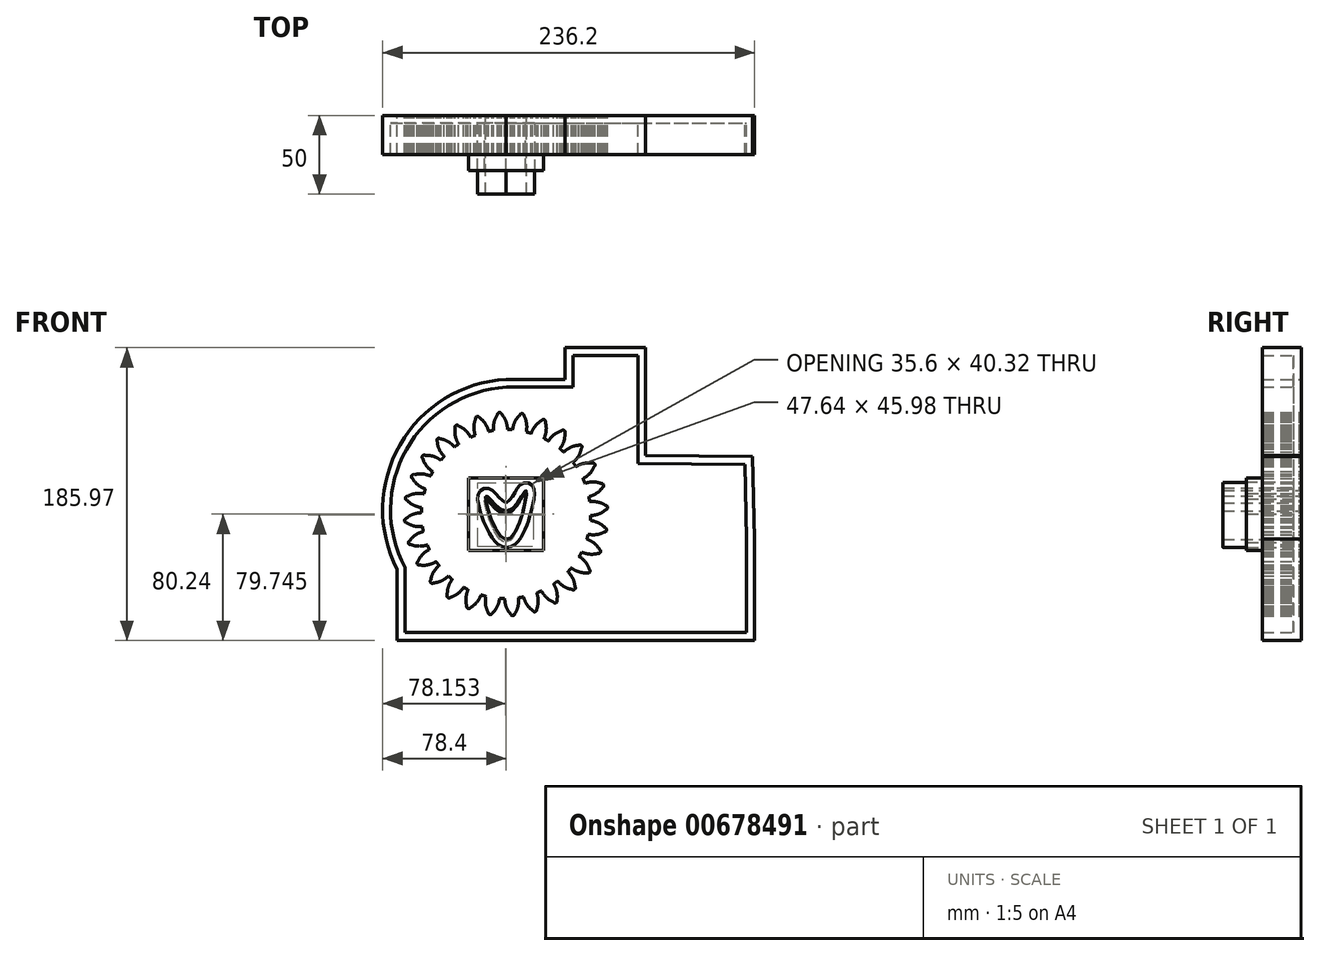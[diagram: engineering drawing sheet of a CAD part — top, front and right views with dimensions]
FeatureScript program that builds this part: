
annotation { "Feature Type Name" : "Feature", "Feature Type Description" : "" }
export const myFeature = defineFeature(function(context is Context, id is Id, definition is map)
    precondition{}
    {
        {
            var Q0;
            Q0=qCreatedBy(makeId("Front.planeOp"),FACE);
            var sketch = newSketch(context, id + "F0", { "sketchPlane" : qUnion([Q0])});
            skCircle(sketch, "E0", {"center": v(0, 0) * mm, "radius": 53.72 * mm});
            skCircle(sketch, "E1", {"center": v(0, 0) * mm, "radius": 58.67 * mm, "construction": true});
            skCircle(sketch, "E2", {"center": v(0, 0) * mm, "radius": 63.5 * mm, "construction": true});
            skLineSegment(sketch, "E3", {"start": v(0, 0) * mm, "end": v(0, 72.67) * mm, "construction": true});
            skLineSegment(sketch, "E4", {"start": v(0, 0) * mm, "end": v(-5.05, 77.02) * mm, "construction": true});
            skLineSegment(sketch, "E5", {"start": v(0, 58.67) * mm, "end": v(-57.47, 58.67) * mm, "construction": true});
            skLineSegment(sketch, "E6", {"start": v(0, 58.67) * mm, "end": v(-61.26, 36.38) * mm, "construction": true});
            skCircle(sketch, "E7", {"center": v(0, 0) * mm, "radius": 55.14 * mm, "construction": true});
            skCircle(sketch, "E8", {"center": v(0, 58.67) * mm, "radius": 14.6 * mm, "construction": true});
            skCircle(sketch, "E9", {"center": v(-13.72, 53.68) * mm, "radius": 14.6 * mm, "construction": true});
            skArc(sketch, "E10", {"start": v(0, 58.67) * mm, "mid": v(-1.19, 61.2) * mm, "end": v(-2.86, 63.44) * mm});
            skArc(sketch, "E11", {"start": v(0.88, 53.71) * mm, "mid": v(0.64, 56.23) * mm, "end": v(0, 58.67) * mm});
            skArc(sketch, "E12.MirrorCS", {"start": v(-7.66, 58.17) * mm, "mid": v(-6.8, 60.83) * mm, "end": v(-5.45, 63.27) * mm});
            skArc(sketch, "E13.MirrorCS", {"start": v(-7.88, 53.14) * mm, "mid": v(-7.98, 55.66) * mm, "end": v(-7.66, 58.17) * mm});
            skArc(sketch, "E14", {"start": v(-2.86, 63.44) * mm, "mid": v(-4.23, 64.55) * mm, "end": v(-5.45, 63.27) * mm});
            skLineSegment(sketch, "E15.bottom", {"start": v(-23.82, 23) * mm, "end": v(23.82, 23) * mm});
            skLineSegment(sketch, "E15.top", {"start": v(-23.82, -23) * mm, "end": v(23.82, -23) * mm});
            skLineSegment(sketch, "E15.left", {"start": v(-23.82, 23) * mm, "end": v(-23.82, -23) * mm});
            skLineSegment(sketch, "E15.right", {"start": v(23.82, 23) * mm, "end": v(23.82, -23) * mm});
            skFitSpline(sketch, "E16", {"points": [v(0, 0) * mm, v(12.25, 13.08) * mm, v(0, -18.04) * mm, v(-13.35, 9.5) * mm, v(0, 0) * mm]});
            skSolve(sketch);
        }
        {
            var Q0;
            {var subQ0=sQuery(id+"F0.wireOp",EDGE,"E0");var subQ1=makeQuery(id+"F0.imprint","INTERSECT",VERTEX,{"derivedFrom":[subQ0,sQuery(id+"F0.wireOp",EDGE,"E11")]});Q0=makeQuery(id+"F0.imprint","IMPRINT",FACE,{"disambiguationData":[TD([[makeQuery(id+"F0.imprint","IMPRINT",EDGE,{"disambiguationData":[TD([[subQ1,-1.0]])],"derivedFrom":subQ0}),1.0]])]});}
            var Q1;
            Q1=makeQuery(id+"F0.imprint","IMPRINT",FACE,{"disambiguationData":[TD([[makeQuery(id+"F0.imprint","IMPRINT",EDGE,{"derivedFrom":sQuery(id+"F0.wireOp",EDGE,"E10")}),1.0]])]});
            extrude(context, id + "F1", {"entities" : qUnion([Q0, Q1]), "depth" : 25 * mm, "offsetDistance" : 25 * mm});
        }
        {
            var Q0;
            Q0=makeQuery(id+"F1.opExtrude","SWEPT_BODY",BODY,{"disambiguationData":[OSD([sQuery(id+"F0.wireOp",EDGE,"E0"),sQuery(id+"F0.wireOp",EDGE,"E10"),sQuery(id+"F0.wireOp",EDGE,"E11"),sQuery(id+"F0.wireOp",EDGE,"E12.MirrorCS"),sQuery(id+"F0.wireOp",EDGE,"E13.MirrorCS"),sQuery(id+"F0.wireOp",EDGE,"E14")])]});
            var Q1;
            Q1=makeQuery(id+"F1.opExtrude","SWEPT_FACE",FACE,{"disambiguationData":[OSD([sQuery(id+"F0.wireOp",EDGE,"E0")])]});
            circularPattern(context, id + "F2", {"entities" : qUnion([Q0]), "axis" : qUnion([Q1]), "angle" : 360 * degree, "instanceCount" : 28, "equalSpace" : true});
        }
        {
            var Q0;
            Q0=makeQuery(id+"F0.imprint","IMPRINT",FACE,{"disambiguationData":[TD([[makeQuery(id+"F0.imprint","IMPRINT",EDGE,{"derivedFrom":sQuery(id+"F0.wireOp",EDGE,"E15.bottom")}),-1.0]])]});
            extrude(context, id + "F3", {"entities" : qUnion([Q0]), "operationType" : NewBodyOperationType.ADD, "depth" : 35 * mm, "offsetDistance" : 25 * mm});
        }
        {
            var Q0;
            Q0=qCreatedBy(makeId("Front.planeOp"),FACE);
            var sketch = newSketch(context, id + "F4", { "sketchPlane" : qUnion([Q0])});
            skLineSegment(sketch, "E17", {"start": v(-69.3, -35.12) * mm, "end": v(-69.3, -80.24) * mm});
            skLineSegment(sketch, "E18", {"start": v(-69.3, -80.24) * mm, "end": v(157.8, -80.24) * mm});
            skLineSegment(sketch, "E19", {"start": v(157.8, -80.24) * mm, "end": v(157.8, -15.79) * mm});
            skArc(sketch, "E20", {"start": v(0, 85.57) * mm, "mid": v(-67.38, 44.02) * mm, "end": v(-69.3, -35.12) * mm});
            skLineSegment(sketch, "E21", {"start": v(0, 85.57) * mm, "end": v(37.45, 85.57) * mm});
            skLineSegment(sketch, "E22", {"start": v(37.45, 85.57) * mm, "end": v(37.45, 105.73) * mm});
            skLineSegment(sketch, "E23", {"start": v(37.45, 105.73) * mm, "end": v(88.7, 105.73) * mm});
            skLineSegment(sketch, "E24", {"start": v(88.7, 105.73) * mm, "end": v(88.7, 37.2) * mm});
            skLineSegment(sketch, "E25", {"start": v(88.7, 37.2) * mm, "end": v(156.65, 36.62) * mm});
            skLineSegment(sketch, "E26", {"start": v(156.65, 36.62) * mm, "end": v(157.8, -15.79) * mm});
            skFitSpline(sketch, "E27", {"points": [v(0.53, 1.9) * mm, v(12.79, 14.97) * mm, v(0.53, -16.14) * mm, v(-12.82, 11.4) * mm, v(0.53, 1.9) * mm]});
            skSolve(sketch);
        }
        {
            var Q0;
            Q0=makeQuery(id+"F4.imprint","IMPRINT",FACE,{"disambiguationData":[TD([[makeQuery(id+"F4.imprint","IMPRINT",EDGE,{"derivedFrom":sQuery(id+"F4.wireOp",EDGE,"E17")}),1.0]])]});
            extrude(context, id + "F5", {"entities" : qUnion([Q0]), "depth" : 50 * mm, "offsetDistance" : 25 * mm});
        }
        {
            var Q0;
            Q0=makeQuery(id+"F5.opExtrude","CAP_FACE",FACE,{"disambiguationData":[OSD([sQuery(id+"F4.wireOp",EDGE,"E17"),sQuery(id+"F4.wireOp",EDGE,"E18"),sQuery(id+"F4.wireOp",EDGE,"E19"),sQuery(id+"F4.wireOp",EDGE,"E20"),sQuery(id+"F4.wireOp",EDGE,"E21"),sQuery(id+"F4.wireOp",EDGE,"E22"),sQuery(id+"F4.wireOp",EDGE,"E23"),sQuery(id+"F4.wireOp",EDGE,"E24"),sQuery(id+"F4.wireOp",EDGE,"E25"),sQuery(id+"F4.wireOp",EDGE,"E26")])],"isStart":false});
            shell(context, id + "F6", {"entities" : qUnion([Q0]), "thickness" : 5 * mm});
        }
        {
            var Q0;
            Q0=makeQuery(id+"F5.opExtrude","CAP_FACE",FACE,{"disambiguationData":[OSD([sQuery(id+"F4.wireOp",EDGE,"E17"),sQuery(id+"F4.wireOp",EDGE,"E18"),sQuery(id+"F4.wireOp",EDGE,"E19"),sQuery(id+"F4.wireOp",EDGE,"E20"),sQuery(id+"F4.wireOp",EDGE,"E21"),sQuery(id+"F4.wireOp",EDGE,"E22"),sQuery(id+"F4.wireOp",EDGE,"E23"),sQuery(id+"F4.wireOp",EDGE,"E24"),sQuery(id+"F4.wireOp",EDGE,"E25"),sQuery(id+"F4.wireOp",EDGE,"E26"),sQuery(id+"F4.wireOp",EDGE,"E27")])],"isStart":false});
            extrude(context, id + "F7", {"entities" : qUnion([Q0]), "operationType" : NewBodyOperationType.REMOVE, "oppositeDirection" : true, "depth" : 25 * mm, "offsetDistance" : 25 * mm});
        }
    });
